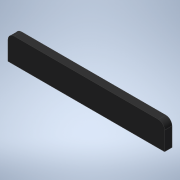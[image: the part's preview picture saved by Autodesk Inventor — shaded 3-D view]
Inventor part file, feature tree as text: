
AUTODESK INVENTOR PART (.ipt)
format: ipt  version: 2020 (Build 240168000, 168)  size: 103,424 bytes
history: native  units: mm
features: other x1, extrude x1, fillet x1
ambient origin geometry x8: Origin, YZ Plane, XZ Plane, XY Plane, X Axis, Y Axis, Z Axis, Center Point
bodies: Body1 (feature_tree)
feature tree (3):
  other  "實體1"
  extrude  "擠出1"  Depth=20.0mm
  fillet  "圓角1"  Radius=126.0mm
